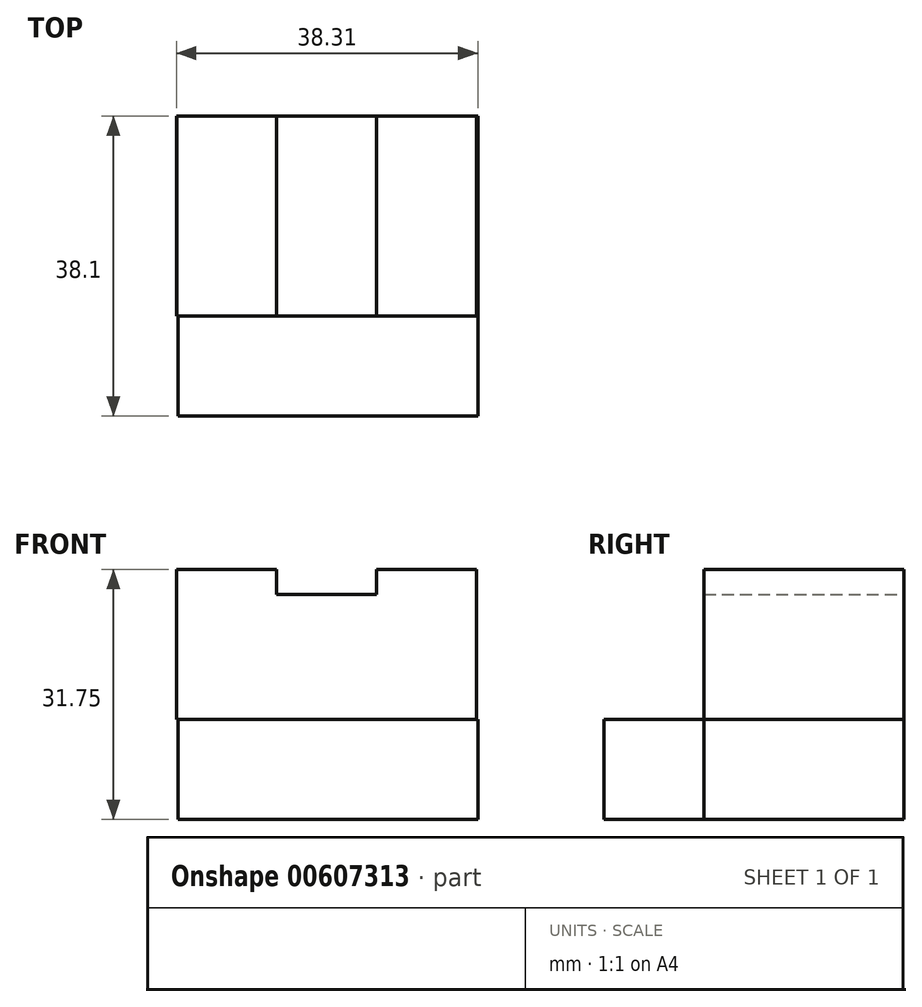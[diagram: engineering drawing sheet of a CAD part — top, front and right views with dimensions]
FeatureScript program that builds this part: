
annotation { "Feature Type Name" : "Feature", "Feature Type Description" : "" }
export const myFeature = defineFeature(function(context is Context, id is Id, definition is map)
    precondition{}
    {
        {
            var Q0;
            Q0=qCreatedBy(makeId("Front.planeOp"),FACE);
            var sketch = newSketch(context, id + "F0", { "sketchPlane" : qUnion([Q0])});
            skLineSegment(sketch, "E0", {"start": v(-18.26, 19.05) * mm, "end": v(-5.56, 19.05) * mm});
            skLineSegment(sketch, "E1", {"start": v(-5.56, 19.05) * mm, "end": v(-5.56, 15.87) * mm});
            skLineSegment(sketch, "E2", {"start": v(-5.56, 15.87) * mm, "end": v(7.14, 15.88) * mm});
            skLineSegment(sketch, "E3", {"start": v(7.14, 15.88) * mm, "end": v(7.14, 19.05) * mm});
            skLineSegment(sketch, "E4", {"start": v(7.14, 19.05) * mm, "end": v(19.84, 19.05) * mm});
            skLineSegment(sketch, "E5", {"start": v(19.84, 19.05) * mm, "end": v(19.84, 0) * mm});
            skLineSegment(sketch, "E6", {"start": v(-18.26, 19.05) * mm, "end": v(-18.26, 0) * mm});
            skLineSegment(sketch, "E7", {"start": v(-18.26, 0) * mm, "end": v(19.84, 0) * mm});
            skSolve(sketch);
        }
        {
            var Q0;
            Q0=qCreatedBy(makeId("Front.planeOp"),FACE);
            var sketch = newSketch(context, id + "F1", { "sketchPlane" : qUnion([Q0])});
            skLineSegment(sketch, "E8", {"start": v(-18.05, 0) * mm, "end": v(-18.05, -12.7) * mm});
            skLineSegment(sketch, "E9", {"start": v(-18.05, -12.7) * mm, "end": v(20.05, -12.7) * mm});
            skLineSegment(sketch, "E10", {"start": v(20.05, -12.7) * mm, "end": v(20.05, 0) * mm});
            skLineSegment(sketch, "E11", {"start": v(-18.05, 0) * mm, "end": v(20.05, 0) * mm});
            skSolve(sketch);
        }
        {
            var Q0;
            Q0 = qSketchRegion(id + "F0", true);
            var Q1;
            Q1 = qSketchRegion(id + "F1", true);
            extrude(context, id + "F2", {"entities" : qUnion([Q0, Q1]), "depth" : 25.4 * mm, "offsetDistance" : 25.4 * mm});
        }
        {
            var Q0;
            Q0 = qSketchRegion(id + "F1", true);
            extrude(context, id + "F3", {"entities" : qUnion([Q0]), "depth" : 38.1 * mm, "offsetDistance" : 25.4 * mm});
        }
    });
